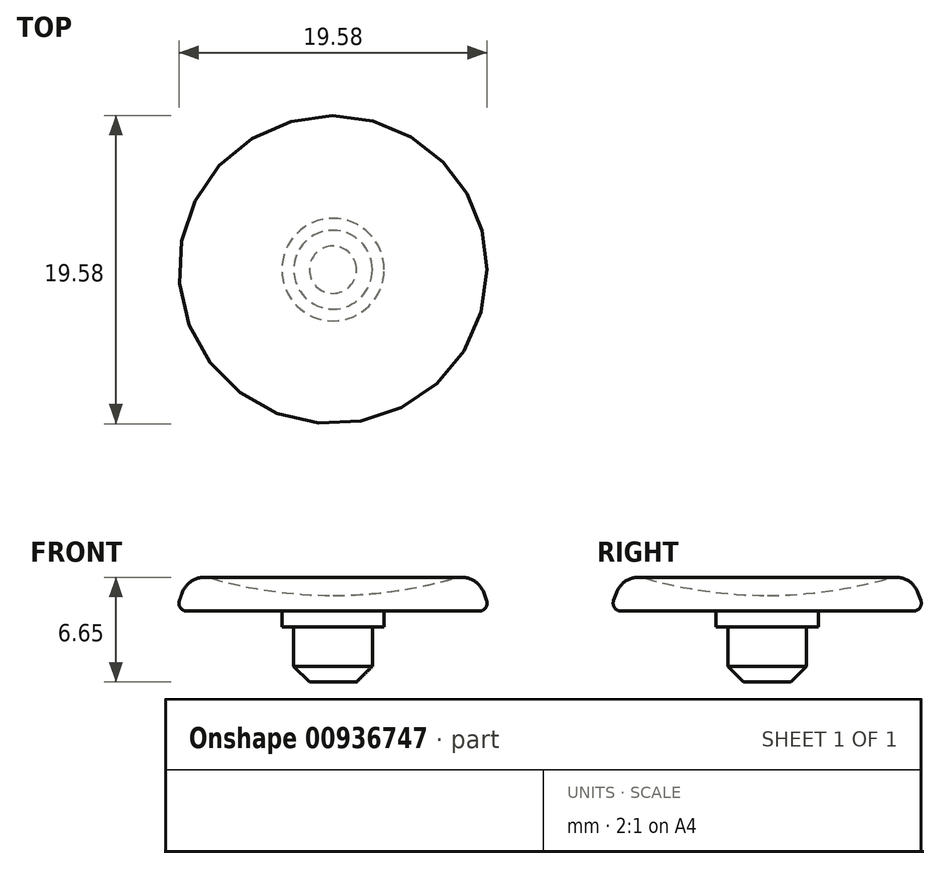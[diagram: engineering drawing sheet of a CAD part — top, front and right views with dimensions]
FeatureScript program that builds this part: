
annotation { "Feature Type Name" : "Feature", "Feature Type Description" : "" }
export const myFeature = defineFeature(function(context is Context, id is Id, definition is map)
    precondition{}
    {
        {
            var Q0;
            Q0=qCreatedBy(makeId("Top.planeOp"),FACE);
            var sketch = newSketch(context, id + "F0", { "sketchPlane" : qUnion([Q0])});
            skCircle(sketch, "E0", {"center": v(0, 0) * mm, "radius": 2.5 * mm});
            skSolve(sketch);
        }
        {
            var Q0;
            Q0=makeQuery(id+"F0.imprint","IMPRINT",FACE,{"disambiguationData":[TD([[makeQuery(id+"F0.imprint","IMPRINT",EDGE,{"derivedFrom":sQuery(id+"F0.wireOp",EDGE,"E0")}),1.0]])]});
            extrude(context, id + "F1", {"entities" : qUnion([Q0]), "oppositeDirection" : true, "depth" : 3.5 * mm, "offsetDistance" : 25 * mm});
        }
        {
            var Q0;
            Q0=makeQuery(id+"F1.opExtrude","CAP_EDGE",EDGE,{"disambiguationData":[OSD([sQuery(id+"F0.wireOp",EDGE,"E0")])],"isStart":false});
            chamfer(context, id + "F2", {"entities" : qUnion([Q0]), "width" : 1 * mm, "tangentPropagation" : true});
        }
        {
            var Q0;
            Q0=qCreatedBy(makeId("Top.planeOp"),FACE);
            var sketch = newSketch(context, id + "F3", { "sketchPlane" : qUnion([Q0])});
            skCircle(sketch, "E1", {"center": v(0, 0) * mm, "radius": 3.25 * mm});
            skSolve(sketch);
        }
        {
            var Q0;
            Q0 = qSketchRegion(id + "F3", true);
            extrude(context, id + "F4", {"entities" : qUnion([Q0]), "operationType" : NewBodyOperationType.ADD, "depth" : 1 * mm, "offsetDistance" : 25 * mm});
        }
        {
            var Q0;
            Q0=qCreatedBy(makeId("Front.planeOp"),FACE);
            var sketch = newSketch(context, id + "F5", { "sketchPlane" : qUnion([Q0])});
            skLineSegment(sketch, "E2", {"start": v(0, 1) * mm, "end": v(10, 1) * mm});
            skLineSegment(sketch, "E3", {"start": v(10, 1) * mm, "end": v(9.08, 3.51) * mm});
            skArc(sketch, "E4", {"start": v(0, 2) * mm, "mid": v(4.6, 2.38) * mm, "end": v(9.08, 3.51) * mm});
            skLineSegment(sketch, "E5", {"start": v(0, 2) * mm, "end": v(0, 1) * mm});
            skLineSegment(sketch, "E6", {"start": v(0, 2) * mm, "end": v(10.07, 2) * mm, "construction": true});
            skSolve(sketch);
        }
        {
            var Q0;
            Q0=makeQuery(id+"F5.imprint","IMPRINT",FACE,{"disambiguationData":[TD([[makeQuery(id+"F5.imprint","IMPRINT",EDGE,{"derivedFrom":sQuery(id+"F5.wireOp",EDGE,"E2")}),1.0]])]});
            var Q1;
            Q1=sQuery(id+"F5.wireOp",EDGE,"E5");
            revolve(context, id + "F6", {"operationType" : NewBodyOperationType.ADD, "surfaceOperationType" : NewSurfaceOperationType.NEW, "entities" : qUnion([Q0]), "axis" : qUnion([Q1]), "revolveType" : RevolveType.FULL});
        }
        {
            var Q0;
            Q0=makeQuery(id+"F6.opRevolve","SWEPT_EDGE",EDGE,{"disambiguationData":[OSD([sQuery(id+"F5.wireOp",EDGE,"E3"),sQuery(id+"F5.wireOp",EDGE,"E4")])]});
            fillet(context, id + "F7", {"entities" : qUnion([Q0]), "radius" : 1.5 * mm, "tangentPropagation" : true, "allowEdgeOverflow" : false});
        }
        {
            var Q0;
            Q0=makeQuery(id+"F6.opRevolve","SWEPT_EDGE",EDGE,{"disambiguationData":[OSD([sQuery(id+"F5.wireOp",EDGE,"E2"),sQuery(id+"F5.wireOp",EDGE,"E3")])]});
            fillet(context, id + "F8", {"entities" : qUnion([Q0]), "radius" : 0.5 * mm, "tangentPropagation" : true, "allowEdgeOverflow" : false});
        }
    });
